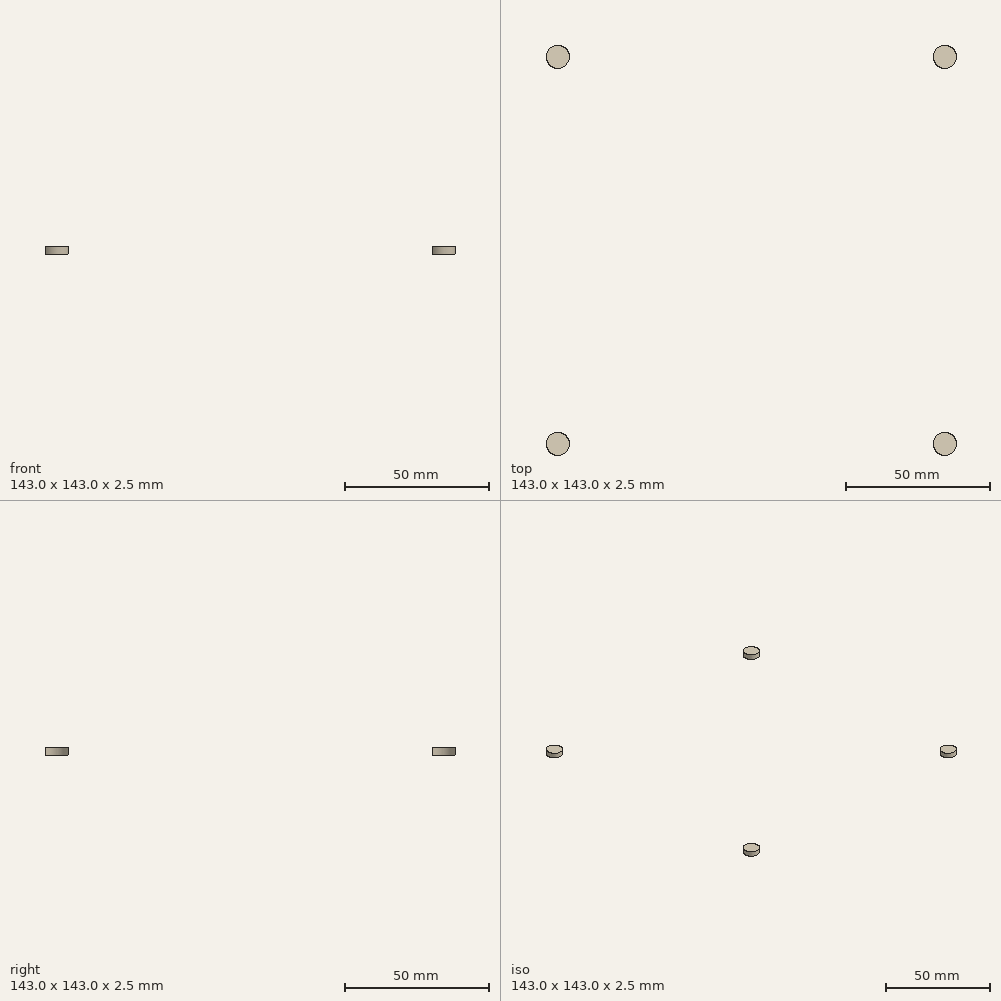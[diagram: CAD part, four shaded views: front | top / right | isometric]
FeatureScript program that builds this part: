
annotation { "Feature Type Name" : "Feature", "Feature Type Description" : "" }
export const myFeature = defineFeature(function(context is Context, id is Id, definition is map)
    precondition{}
    {
        {
            var Q0;
            Q0=qCreatedBy(makeId("Top.planeOp"),FACE);
            var sketch = newSketch(context, id + "F0", { "sketchPlane" : qUnion([Q0])});
            skCircle(sketch, "E0", {"center": v(0, 0) * mm, "radius": 4 * mm});
            skCircle(sketch, "E1", {"center": v(0, 135) * mm, "radius": 4 * mm});
            skCircle(sketch, "E2", {"center": v(135, 135) * mm, "radius": 4 * mm});
            skCircle(sketch, "E3", {"center": v(135, 0) * mm, "radius": 4 * mm});
            skSolve(sketch);
        }
        {
            var Q0;
            Q0 = qSketchRegion(id + "F0", true);
            extrude(context, id + "F1", {"entities" : qUnion([Q0]), "depth" : 2.54 * mm, "offsetDistance" : 25.4 * mm});
        }
    });
